FCSTD DOCUMENT  (FreeCAD 0.19R14555 (Git shallow))
Label: KeyLock
License: All rights reserved
LicenseURL: http://en.wikipedia.org/wiki/All_rights_reserved
objects: Sketcher::SketchObject×1, PartDesign::Body×1, App::Part×1
note: 2 computed .brp shape members not serialized (recipe doc carries the construction recipe); baked Part::Feature solids carry a one-line shape summary decoded from their .brp

FEATURE [Sketcher::SketchObject] Sketch
  FullyConstrained = true
  MapMode = 5
  Support = -> [XY_Plane001]
  sketch-geometry (7):
    g0: LineSegment StartX=0 StartY=75 StartZ=0 EndX=100 EndY=75 EndZ=0
    g1: LineSegment StartX=100 StartY=75 StartZ=0 EndX=100 EndY=0 EndZ=0
    g2: LineSegment StartX=100 StartY=0 StartZ=0 EndX=0 EndY=0 EndZ=0
    g3: LineSegment StartX=0 StartY=0 StartZ=0 EndX=0 EndY=75 EndZ=0
    g4: Circle CenterX=50 CenterY=20 CenterZ=0 NormalX=0 NormalY=0 NormalZ=1 AngleXU=0 Radius=15
    g5: LineSegment StartX=38.8197 StartY=10 StartZ=0 EndX=38.8197 EndY=0 EndZ=0
    g6: LineSegment StartX=61.1803 StartY=10 StartZ=0 EndX=61.1803 EndY=0 EndZ=0
  constraints (22):
    c: Coincident(g0,g1)
    c: Coincident(g1,g2)
    c: Coincident(g2,g3)
    c: Coincident(g3,g0)
    c: Horizontal(g0)
    c: Vertical(g1)
    c: Vertical(g3)
    c: Coincident(g2,g-1)
    c: DistanceY(g3,g3) = 75
    c: DistanceX(g2,g2) = 100
    c: DistanceY(g2,g4) = 20
    c: DistanceX(g2,g4) = 50
    c: Diameter(g4) = 30
    c: PointOnObject(g5,g4)
    c: PointOnObject(g5,g2)
    c: Vertical(g5)
    c: PointOnObject(g6,g4)
    c: PointOnObject(g6,g2)
    c: DistanceY(g5,g5) = 10
    c: DistanceY(g6,g6) = 10
    c: Perpendicular(g2,g6)
    c: Horizontal(g2)
FEATURE [PartDesign::Body] Body
  Group = -> [Sketch]
  Origin = -> Origin001
FEATURE [App::Part] Part
  Group = -> [Body]
  Origin = -> Origin
